AUTODESK INVENTOR PART (.ipt)
format: ipt  version: 2011 SP1 (Build 150282100, 282)  size: 67,072 bytes
history: native  units: mm (DEFAULTED — no unit token found)
features: other x14, plane x1, sketch x1, sweep x1
ambient origin geometry x8: Origin, YZ Plane, XZ Plane, XY Plane, X Axis, Y Axis, Z Axis, Center Point
feature tree (17):
  other  "Work Point1"
  other  "Work Point2"
  other  "Cable1:1"
  other  "Work Point3"
  other  "Work Point4"
  other  "Cable1:2"
  other  "Work Point5"
  other  "Work Point6"
  other  "Cable1:3"
  other  "Work Point7"
  other  "Work Point8"
  other  "Segment1"
  plane  "Work Plane1"
  other  "Work Point9"
  sketch  "Sketch1"  dims[d0=0.0mm]
  other  "Srf1"
  sweep  "SweepSrf1"
